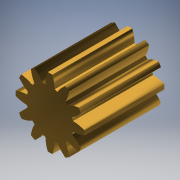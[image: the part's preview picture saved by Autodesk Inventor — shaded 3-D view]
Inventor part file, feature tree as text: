
AUTODESK INVENTOR PART (.ipt)
format: ipt  version: 2019 (Build 230136000, 136)  size: 201,216 bytes
history: native  units: mm (DEFAULTED — no unit token found)
features: plane x3, other x3, sketch x2, extrude x1
ambient origin geometry x8: Origin, YZ Plane, XZ Plane, XY Plane, X Axis, Y Axis, Z Axis, Center Point
bodies: Solid1 (feature_tree)
feature tree (9):
  extrude  "Extrusion1"  Depth=3.25mm TaperAngle=0.0deg
  plane  "Work Plane2"
  plane  "Work Plane8"
  plane  "Work Plane9"
  other  "Spur Gear"
  sketch  "Sketch1"  dims[d0=2.799202mm d1=3.25mm d2=0.0mm]
  sketch  "Sketch2"  dims[d3=2.39mm d4=10.0mm d5=0.0mm d16=5.975mm d17=0.0mm d34=15.0deg d39=0.0mm d41=0.0mm d43=5.975mm d46=5.975mm d47=0.0mm d48=0.0mm]
  other  "Srf1"
  other  "Pitch Diameter"
